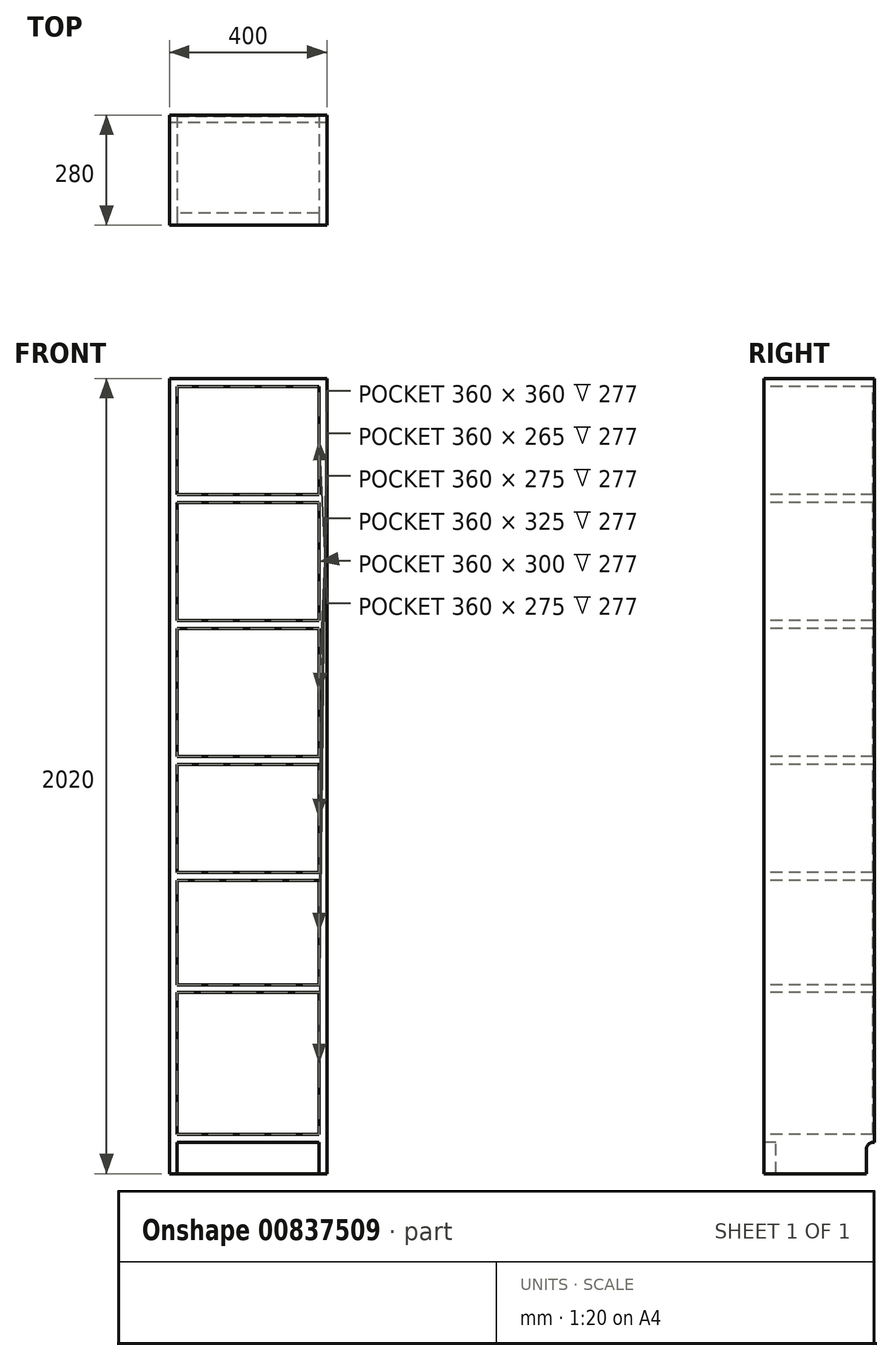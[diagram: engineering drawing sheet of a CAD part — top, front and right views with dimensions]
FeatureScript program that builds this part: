
annotation { "Feature Type Name" : "Feature", "Feature Type Description" : "" }
export const myFeature = defineFeature(function(context is Context, id is Id, definition is map)
    precondition{}
    {
        {
            var Q0;
            Q0=qCreatedBy(makeId("Top.planeOp"),FACE);
            var sketch = newSketch(context, id + "F0", { "sketchPlane" : qUnion([Q0])});
            skLineSegment(sketch, "E0.bottom", {"start": v(200, 0) * mm, "end": v(-200, 0) * mm});
            skLineSegment(sketch, "E0.top", {"start": v(200, -280) * mm, "end": v(-200, -280) * mm});
            skLineSegment(sketch, "E0.left", {"start": v(200, 0) * mm, "end": v(200, -280) * mm});
            skLineSegment(sketch, "E0.right", {"start": v(-200, 0) * mm, "end": v(-200, -280) * mm});
            skLineSegment(sketch, "E1", {"start": v(0, 0) * mm, "end": v(0, -280) * mm, "construction": true});
            skSolve(sketch);
        }
        {
            var Q0;
            Q0=makeQuery(id+"F0.imprint","IMPRINT",FACE,{"disambiguationData":[TD([[makeQuery(id+"F0.imprint","IMPRINT",EDGE,{"derivedFrom":sQuery(id+"F0.wireOp",EDGE,"E0.bottom")}),1.0]])]});
            extrude(context, id + "F1", {"entities" : qUnion([Q0]), "depth" : 2020 * mm, "offsetDistance" : 25 * mm});
        }
        {
            var Q0;
            Q0=qCreatedBy(makeId("Front.planeOp"),FACE);
            cPlane(context, id + "F2", {"entities" : qUnion([Q0]), "cplaneType" : CPlaneType.OFFSET, "offset" : 3 * mm, "width" : 150 * mm, "height" : 150 * mm});
        }
        {
            var Q0;
            Q0=makeQuery(id+"F1.opExtrude","SWEPT_FACE",FACE,{"disambiguationData":[OSD([sQuery(id+"F0.wireOp",EDGE,"E0.top")])]});
            var sketch = newSketch(context, id + "F3", { "sketchPlane" : qUnion([Q0])});
            skLineSegment(sketch, "E2", {"start": v(0, 0) * mm, "end": v(0, 2020) * mm, "construction": true});
            skLineSegment(sketch, "E3.bottom", {"start": v(180, 2000) * mm, "end": v(-180, 2000) * mm});
            skLineSegment(sketch, "E3.top", {"start": v(180, 1725) * mm, "end": v(-180, 1725) * mm});
            skLineSegment(sketch, "E3.left", {"start": v(180, 2000) * mm, "end": v(180, 1725) * mm});
            skLineSegment(sketch, "E3.right", {"start": v(-180, 2000) * mm, "end": v(-180, 1725) * mm});
            skPoint(sketch, "E3.middle", {"position": v(0, 1862.5) * mm});
            skLineSegment(sketch, "E4.bottom", {"start": v(180, 2000) * mm, "end": v(200, 2000) * mm, "construction": true});
            skLineSegment(sketch, "E4.top", {"start": v(180, 2020) * mm, "end": v(200, 2020) * mm, "construction": true});
            skLineSegment(sketch, "E4.left", {"start": v(180, 2000) * mm, "end": v(180, 2020) * mm, "construction": true});
            skLineSegment(sketch, "E4.right", {"start": v(200, 2000) * mm, "end": v(200, 2020) * mm, "construction": true});
            skLineSegment(sketch, "E5.bottom", {"start": v(180, 1705) * mm, "end": v(-180, 1705) * mm});
            skLineSegment(sketch, "E5.top", {"start": v(180, 1405) * mm, "end": v(-180, 1405) * mm});
            skLineSegment(sketch, "E5.left", {"start": v(180, 1705) * mm, "end": v(180, 1405) * mm});
            skLineSegment(sketch, "E5.right", {"start": v(-180, 1705) * mm, "end": v(-180, 1405) * mm});
            skPoint(sketch, "E5.middle", {"position": v(0, 1555) * mm});
            skLineSegment(sketch, "E6", {"start": v(180, 1705) * mm, "end": v(180, 1725) * mm, "construction": true});
            skLineSegment(sketch, "E7.bottom", {"start": v(180, 1385) * mm, "end": v(-180, 1385) * mm});
            skLineSegment(sketch, "E7.top", {"start": v(180, 1060) * mm, "end": v(-180, 1060) * mm});
            skLineSegment(sketch, "E7.left", {"start": v(180, 1385) * mm, "end": v(180, 1060) * mm});
            skLineSegment(sketch, "E7.right", {"start": v(-180, 1385) * mm, "end": v(-180, 1060) * mm});
            skPoint(sketch, "E7.middle", {"position": v(0, 1222.5) * mm});
            skLineSegment(sketch, "E8", {"start": v(180, 1385) * mm, "end": v(180, 1405) * mm, "construction": true});
            skLineSegment(sketch, "E9.bottom", {"start": v(180, 1040) * mm, "end": v(-180, 1040) * mm});
            skLineSegment(sketch, "E9.top", {"start": v(180, 765) * mm, "end": v(-180, 765) * mm});
            skLineSegment(sketch, "E9.left", {"start": v(180, 1040) * mm, "end": v(180, 765) * mm});
            skLineSegment(sketch, "E9.right", {"start": v(-180, 1040) * mm, "end": v(-180, 765) * mm});
            skPoint(sketch, "E9.middle", {"position": v(0, 902.5) * mm});
            skLineSegment(sketch, "E10.bottom", {"start": v(180, 745) * mm, "end": v(-180, 745) * mm});
            skLineSegment(sketch, "E10.top", {"start": v(180, 480) * mm, "end": v(-180, 480) * mm});
            skLineSegment(sketch, "E10.left", {"start": v(180, 745) * mm, "end": v(180, 480) * mm});
            skLineSegment(sketch, "E10.right", {"start": v(-180, 745) * mm, "end": v(-180, 480) * mm});
            skPoint(sketch, "E10.middle", {"position": v(0, 612.5) * mm});
            skLineSegment(sketch, "E11", {"start": v(180, 745) * mm, "end": v(180, 765) * mm, "construction": true});
            skLineSegment(sketch, "E12", {"start": v(180, 1040) * mm, "end": v(180, 1060) * mm, "construction": true});
            skLineSegment(sketch, "E13.bottom", {"start": v(180, 460) * mm, "end": v(-180, 460) * mm});
            skLineSegment(sketch, "E13.top", {"start": v(180, 100) * mm, "end": v(-180, 100) * mm});
            skLineSegment(sketch, "E13.left", {"start": v(180, 460) * mm, "end": v(180, 100) * mm});
            skLineSegment(sketch, "E13.right", {"start": v(-180, 460) * mm, "end": v(-180, 100) * mm});
            skPoint(sketch, "E13.middle", {"position": v(0, 280) * mm});
            skLineSegment(sketch, "E14", {"start": v(180, 460) * mm, "end": v(180, 480) * mm, "construction": true});
            skSolve(sketch);
        }
        {
            var Q0;
            Q0=makeQuery(id+"F3.imprint","IMPRINT",FACE,{"disambiguationData":[TD([[makeQuery(id+"F3.imprint","IMPRINT",EDGE,{"derivedFrom":sQuery(id+"F3.wireOp",EDGE,"E3.bottom")}),1.0]])]});
            var Q1;
            Q1=makeQuery(id+"F3.imprint","IMPRINT",FACE,{"disambiguationData":[TD([[makeQuery(id+"F3.imprint","IMPRINT",EDGE,{"derivedFrom":sQuery(id+"F3.wireOp",EDGE,"E5.bottom")}),1.0]])]});
            var Q2;
            Q2=makeQuery(id+"F3.imprint","IMPRINT",FACE,{"disambiguationData":[TD([[makeQuery(id+"F3.imprint","IMPRINT",EDGE,{"derivedFrom":sQuery(id+"F3.wireOp",EDGE,"E7.bottom")}),1.0]])]});
            var Q3;
            Q3=makeQuery(id+"F3.imprint","IMPRINT",FACE,{"disambiguationData":[TD([[makeQuery(id+"F3.imprint","IMPRINT",EDGE,{"derivedFrom":sQuery(id+"F3.wireOp",EDGE,"E9.bottom")}),1.0]])]});
            var Q4;
            Q4=makeQuery(id+"F3.imprint","IMPRINT",FACE,{"disambiguationData":[TD([[makeQuery(id+"F3.imprint","IMPRINT",EDGE,{"derivedFrom":sQuery(id+"F3.wireOp",EDGE,"E10.bottom")}),1.0]])]});
            var Q5;
            Q5=makeQuery(id+"F3.imprint","IMPRINT",FACE,{"disambiguationData":[TD([[makeQuery(id+"F3.imprint","IMPRINT",EDGE,{"derivedFrom":sQuery(id+"F3.wireOp",EDGE,"E13.bottom")}),1.0]])]});
            var Q6;
            Q6=qCreatedBy(id+"F2.planeOp",FACE);
            extrude(context, id + "F4", {"entities" : qUnion([Q0, Q1, Q2, Q3, Q4, Q5]), "operationType" : NewBodyOperationType.REMOVE, "endBound" : BoundingType.UP_TO_SURFACE, "oppositeDirection" : true, "depth" : 25 * mm, "endBoundEntityFace" : qUnion([Q6]), "offsetDistance" : 25 * mm});
        }
        {
            var Q0;
            Q0=makeQuery(id+"F1.opExtrude","SWEPT_FACE",FACE,{"disambiguationData":[OSD([sQuery(id+"F0.wireOp",EDGE,"E0.right")])]});
            var sketch = newSketch(context, id + "F5", { "sketchPlane" : qUnion([Q0])});
            skLineSegment(sketch, "E15.bottom", {"start": v(0, 0) * mm, "end": v(20, 0) * mm});
            skLineSegment(sketch, "E15.top", {"start": v(0, 60) * mm, "end": v(20, 60) * mm, "construction": true});
            skLineSegment(sketch, "E15.left", {"start": v(0, 0) * mm, "end": v(0, 60) * mm, "construction": true});
            skLineSegment(sketch, "E15.right", {"start": v(20, 0) * mm, "end": v(20, 60) * mm});
            skArc(sketch, "E16", {"start": v(20, 60) * mm, "mid": v(14.14, 74.14) * mm, "end": v(0, 80) * mm});
            skLineSegment(sketch, "E17", {"start": v(0, 0) * mm, "end": v(0, 80) * mm});
            skSolve(sketch);
        }
        {
            var Q0;
            Q0=makeQuery(id+"F5.imprint","IMPRINT",FACE,{"disambiguationData":[TD([[makeQuery(id+"F5.imprint","IMPRINT",EDGE,{"derivedFrom":sQuery(id+"F5.wireOp",EDGE,"E15.bottom")}),1.0]])]});
            extrude(context, id + "F6", {"entities" : qUnion([Q0]), "operationType" : NewBodyOperationType.REMOVE, "endBound" : BoundingType.THROUGH_ALL, "oppositeDirection" : true, "depth" : 25 * mm, "offsetDistance" : 25 * mm});
        }
        {
            var Q0;
            Q0=makeQuery(id+"F1.opExtrude","SWEPT_FACE",FACE,{"disambiguationData":[OSD([sQuery(id+"F0.wireOp",EDGE,"E0.top")])]});
            var sketch = newSketch(context, id + "F7", { "sketchPlane" : qUnion([Q0])});
            skLineSegment(sketch, "E18.bottom", {"start": v(-180, 0) * mm, "end": v(180, 0) * mm});
            skLineSegment(sketch, "E18.top", {"start": v(-180, 80) * mm, "end": v(180, 80) * mm});
            skLineSegment(sketch, "E18.left", {"start": v(-180, 0) * mm, "end": v(-180, 80) * mm});
            skLineSegment(sketch, "E18.right", {"start": v(180, 0) * mm, "end": v(180, 80) * mm});
            skLineSegment(sketch, "E19", {"start": v(180, 80) * mm, "end": v(180, 100) * mm, "construction": true});
            skLineSegment(sketch, "E20", {"start": v(180, 0) * mm, "end": v(200, 0) * mm, "construction": true});
            skSolve(sketch);
        }
        {
            var Q0;
            Q0=makeQuery(id+"F7.imprint","IMPRINT",FACE,{"disambiguationData":[TD([[makeQuery(id+"F7.imprint","IMPRINT",EDGE,{"derivedFrom":sQuery(id+"F7.wireOp",EDGE,"E18.bottom")}),-1.0]])]});
            extrude(context, id + "F8", {"entities" : qUnion([Q0]), "operationType" : NewBodyOperationType.REMOVE, "oppositeDirection" : true, "depth" : 30 * mm, "offsetDistance" : 25 * mm});
        }
    });
